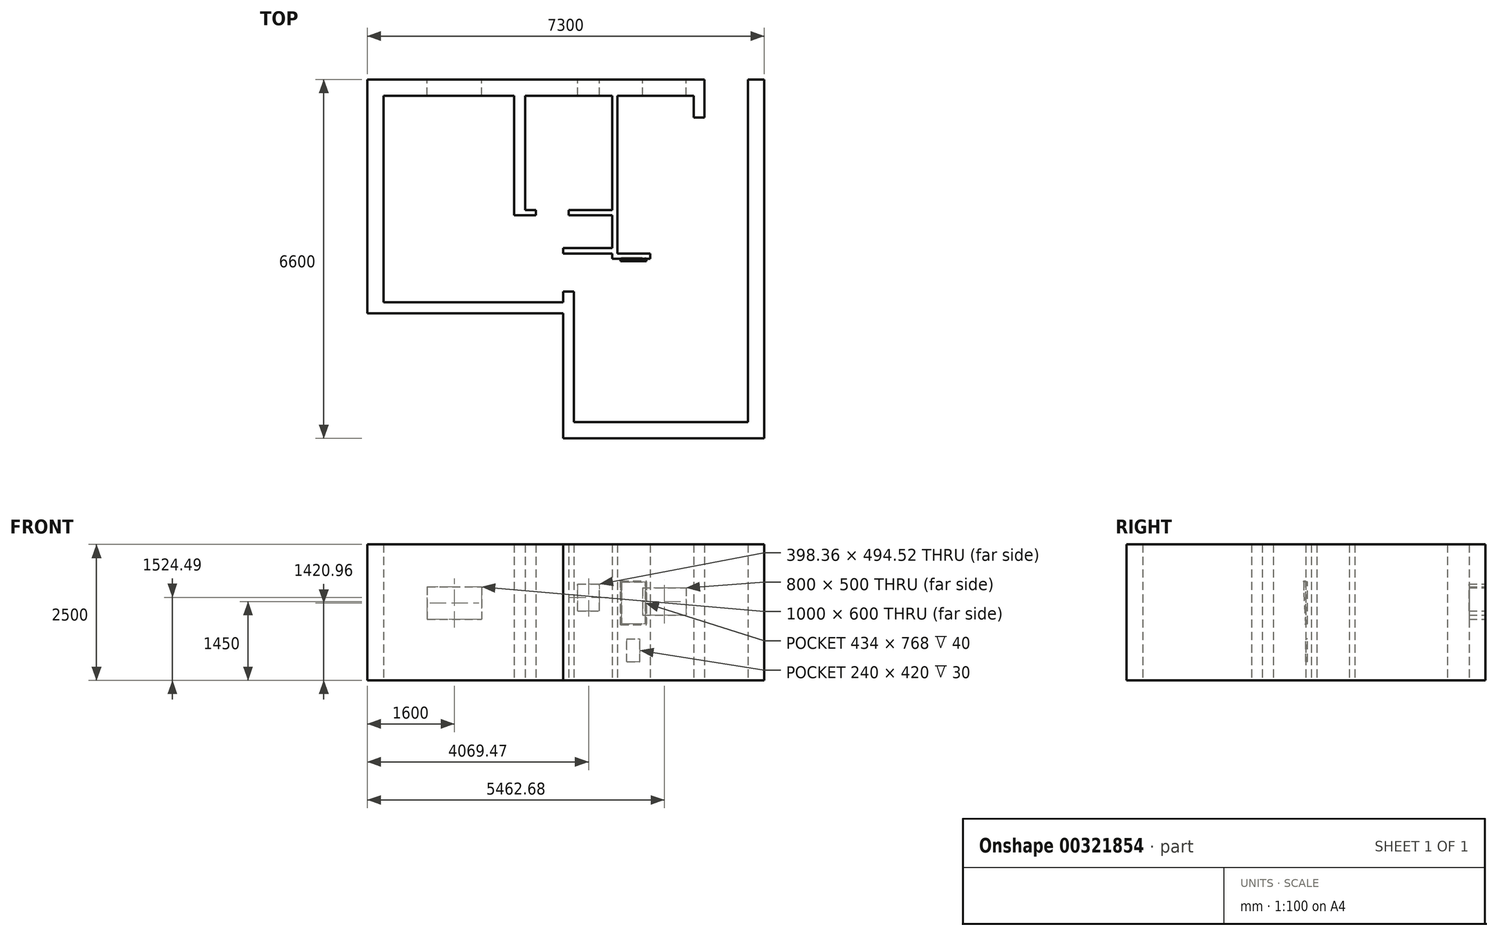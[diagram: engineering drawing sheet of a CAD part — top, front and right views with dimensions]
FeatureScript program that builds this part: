
annotation { "Feature Type Name" : "Feature", "Feature Type Description" : "" }
export const myFeature = defineFeature(function(context is Context, id is Id, definition is map)
    precondition{}
    {
        {
            var Q0;
            Q0=qCreatedBy(makeId("Top.planeOp"),FACE);
            var sketch = newSketch(context, id + "F0", { "sketchPlane" : qUnion([Q0])});
            skLineSegment(sketch, "E0.bottom", {"start": v(0, 0) * mm, "end": v(300, 0) * mm});
            skLineSegment(sketch, "E0.top", {"start": v(0, -5600) * mm, "end": v(300, -5600) * mm});
            skLineSegment(sketch, "E0.left", {"start": v(0, 0) * mm, "end": v(0, -5600) * mm});
            skLineSegment(sketch, "E0.right", {"start": v(300, 0) * mm, "end": v(300, -5600) * mm});
            skLineSegment(sketch, "E1.bottom", {"start": v(300, -5600) * mm, "end": v(-3200, -5600) * mm});
            skLineSegment(sketch, "E1.top", {"start": v(300, -5900) * mm, "end": v(-3200, -5900) * mm});
            skLineSegment(sketch, "E1.left", {"start": v(300, -5600) * mm, "end": v(300, -5900) * mm});
            skLineSegment(sketch, "E1.right", {"start": v(-3200, -5600) * mm, "end": v(-3200, -5900) * mm});
            skLineSegment(sketch, "E2.bottom", {"start": v(-3200, -5900) * mm, "end": v(-3400, -5900) * mm});
            skLineSegment(sketch, "E2.top", {"start": v(-3200, -3200) * mm, "end": v(-3400, -3200) * mm});
            skLineSegment(sketch, "E2.left", {"start": v(-3200, -5900) * mm, "end": v(-3200, -3200) * mm});
            skLineSegment(sketch, "E2.right", {"start": v(-3400, -5900) * mm, "end": v(-3400, -3200) * mm});
            skLineSegment(sketch, "E3.bottom", {"start": v(-3400, -3400) * mm, "end": v(-6700, -3400) * mm});
            skLineSegment(sketch, "E3.top", {"start": v(-3400, -3600) * mm, "end": v(-6700, -3600) * mm});
            skLineSegment(sketch, "E3.left", {"start": v(-3400, -3400) * mm, "end": v(-3400, -3600) * mm});
            skLineSegment(sketch, "E3.right", {"start": v(-6700, -3400) * mm, "end": v(-6700, -3600) * mm});
            skLineSegment(sketch, "E4.bottom", {"start": v(-6700, -3600) * mm, "end": v(-7000, -3600) * mm});
            skLineSegment(sketch, "E4.top", {"start": v(-6700, 400) * mm, "end": v(-7000, 400) * mm});
            skLineSegment(sketch, "E4.left", {"start": v(-6700, -3600) * mm, "end": v(-6700, 400) * mm});
            skLineSegment(sketch, "E4.right", {"start": v(-7000, -3600) * mm, "end": v(-7000, 400) * mm});
            skLineSegment(sketch, "E5.bottom", {"start": v(-7000, 400) * mm, "end": v(-1000, 400) * mm});
            skLineSegment(sketch, "E5.top", {"start": v(-7000, 700) * mm, "end": v(-1000, 700) * mm});
            skLineSegment(sketch, "E5.left", {"start": v(-7000, 400) * mm, "end": v(-7000, 700) * mm});
            skLineSegment(sketch, "E5.right", {"start": v(-1000, 400) * mm, "end": v(-1000, 700) * mm});
            skLineSegment(sketch, "E6.bottom", {"start": v(-4300, 400) * mm, "end": v(-4100, 400) * mm});
            skLineSegment(sketch, "E6.top", {"start": v(-4300, -1800) * mm, "end": v(-4100, -1800) * mm});
            skLineSegment(sketch, "E6.left", {"start": v(-4300, 400) * mm, "end": v(-4300, -1800) * mm});
            skLineSegment(sketch, "E6.right", {"start": v(-4100, 400) * mm, "end": v(-4100, -1800) * mm});
            skLineSegment(sketch, "E7.bottom", {"start": v(-1000, 700) * mm, "end": v(-800, 700) * mm});
            skLineSegment(sketch, "E7.top", {"start": v(-1000, 0) * mm, "end": v(-800, 0) * mm});
            skLineSegment(sketch, "E7.left", {"start": v(-1000, 700) * mm, "end": v(-1000, 0) * mm});
            skLineSegment(sketch, "E7.right", {"start": v(-800, 700) * mm, "end": v(-800, 0) * mm});
            skLineSegment(sketch, "E8.bottom", {"start": v(-4300, -1800) * mm, "end": v(-3900, -1800) * mm});
            skLineSegment(sketch, "E8.top", {"start": v(-4300, -1700) * mm, "end": v(-3900, -1700) * mm});
            skLineSegment(sketch, "E8.left", {"start": v(-4300, -1800) * mm, "end": v(-4300, -1700) * mm});
            skLineSegment(sketch, "E8.right", {"start": v(-3900, -1800) * mm, "end": v(-3900, -1700) * mm});
            skLineSegment(sketch, "E9.bottom", {"start": v(-3300, -1800) * mm, "end": v(-2500, -1800) * mm});
            skLineSegment(sketch, "E9.top", {"start": v(-3300, -1700) * mm, "end": v(-2500, -1700) * mm});
            skLineSegment(sketch, "E9.left", {"start": v(-3300, -1800) * mm, "end": v(-3300, -1700) * mm});
            skLineSegment(sketch, "E9.right", {"start": v(-2500, -1800) * mm, "end": v(-2500, -1700) * mm});
            skLineSegment(sketch, "E10.bottom", {"start": v(-2500, -2500) * mm, "end": v(-2400, -2500) * mm});
            skLineSegment(sketch, "E10.top", {"start": v(-2500, 400) * mm, "end": v(-2400, 400) * mm});
            skLineSegment(sketch, "E10.left", {"start": v(-2500, -2500) * mm, "end": v(-2500, 400) * mm});
            skLineSegment(sketch, "E10.right", {"start": v(-2400, -2500) * mm, "end": v(-2400, 400) * mm});
            skLineSegment(sketch, "E11.bottom", {"start": v(-2500, -2500) * mm, "end": v(-3400, -2500) * mm});
            skLineSegment(sketch, "E11.top", {"start": v(-2500, -2400) * mm, "end": v(-3400, -2400) * mm});
            skLineSegment(sketch, "E11.left", {"start": v(-2500, -2500) * mm, "end": v(-2500, -2400) * mm});
            skLineSegment(sketch, "E11.right", {"start": v(-3400, -2500) * mm, "end": v(-3400, -2400) * mm});
            skLineSegment(sketch, "E12.bottom", {"start": v(-2500, -2500) * mm, "end": v(-1800, -2500) * mm});
            skLineSegment(sketch, "E12.top", {"start": v(-2500, -2600) * mm, "end": v(-1800, -2600) * mm});
            skLineSegment(sketch, "E12.left", {"start": v(-2500, -2500) * mm, "end": v(-2500, -2600) * mm});
            skLineSegment(sketch, "E12.right", {"start": v(-1800, -2500) * mm, "end": v(-1800, -2600) * mm});
            skLineSegment(sketch, "E13.top", {"start": v(0, 700) * mm, "end": v(300, 700) * mm});
            skLineSegment(sketch, "E13.left", {"start": v(0, 0) * mm, "end": v(0, 700) * mm});
            skLineSegment(sketch, "E13.right", {"start": v(300, 0) * mm, "end": v(300, 700) * mm});
            skSolve(sketch);
        }
        {
            var Q0;
            {var subQ3=sQuery(id+"F0.wireOp",EDGE,"E4.top");Q0=makeQuery(id+"F0.imprint","IMPRINT",FACE,{"disambiguationData":[TD([[makeQuery(id+"F0.imprint","IMPRINT",EDGE,{"derivedFrom":subQ3}),-1.0]])]});}
            var Q1;
            Q1=makeQuery(id+"F0.imprint","IMPRINT",FACE,{"disambiguationData":[TD([[makeQuery(id+"F0.imprint","IMPRINT",EDGE,{"derivedFrom":sQuery(id+"F0.wireOp",EDGE,"E3.right")}),-1.0]])]});
            var Q2;
            {var subQ0=sQuery(id+"F0.wireOp",EDGE,"E3.bottom");Q2=makeQuery(id+"F0.imprint","IMPRINT",FACE,{"disambiguationData":[TD([[makeQuery(id+"F0.imprint","IMPRINT",EDGE,{"derivedFrom":subQ0}),1.0]])]});}
            var Q3;
            Q3=makeQuery(id+"F0.imprint","IMPRINT",FACE,{"disambiguationData":[TD([[makeQuery(id+"F0.imprint","IMPRINT",EDGE,{"derivedFrom":sQuery(id+"F0.wireOp",EDGE,"E1.right")}),-1.0]])]});
            var Q4;
            Q4=makeQuery(id+"F0.imprint","IMPRINT",FACE,{"disambiguationData":[TD([[makeQuery(id+"F0.imprint","IMPRINT",EDGE,{"derivedFrom":sQuery(id+"F0.wireOp",EDGE,"E0.top")}),-1.0]])]});
            var Q5;
            Q5=makeQuery(id+"F0.imprint","IMPRINT",FACE,{"disambiguationData":[TD([[makeQuery(id+"F0.imprint","IMPRINT",EDGE,{"derivedFrom":sQuery(id+"F0.wireOp",EDGE,"E0.bottom")}),-1.0]])]});
            var Q6;
            Q6=makeQuery(id+"F0.imprint","IMPRINT",FACE,{"disambiguationData":[TD([[makeQuery(id+"F0.imprint","IMPRINT",EDGE,{"derivedFrom":sQuery(id+"F0.wireOp",EDGE,"E0.bottom")}),1.0]])]});
            var Q7;
            Q7=makeQuery(id+"F0.imprint","IMPRINT",FACE,{"disambiguationData":[TD([[makeQuery(id+"F0.imprint","IMPRINT",EDGE,{"derivedFrom":sQuery(id+"F0.wireOp",EDGE,"E5.right")}),-1.0]])]});
            var Q8;
            Q8=makeQuery(id+"F0.imprint","IMPRINT",FACE,{"disambiguationData":[TD([[makeQuery(id+"F0.imprint","IMPRINT",EDGE,{"derivedFrom":sQuery(id+"F0.wireOp",EDGE,"E10.bottom")}),-1.0]])]});
            var Q9;
            {var subQ1=sQuery(id+"F0.wireOp",EDGE,"E9.right");Q9=makeQuery(id+"F0.imprint","IMPRINT",FACE,{"disambiguationData":[TD([[makeQuery(id+"F0.imprint","IMPRINT",EDGE,{"derivedFrom":subQ1}),-1.0]])]});}
            var Q10;
            {var subQ0=sQuery(id+"F0.wireOp",EDGE,"E11.bottom");Q10=makeQuery(id+"F0.imprint","IMPRINT",FACE,{"disambiguationData":[TD([[makeQuery(id+"F0.imprint","IMPRINT",EDGE,{"derivedFrom":subQ0}),-1.0]])]});}
            var Q11;
            Q11=makeQuery(id+"F0.imprint","IMPRINT",FACE,{"disambiguationData":[TD([[makeQuery(id+"F0.imprint","IMPRINT",EDGE,{"derivedFrom":sQuery(id+"F0.wireOp",EDGE,"E9.bottom")}),1.0]])]});
            var Q12;
            {var subQ0=sQuery(id+"F0.wireOp",EDGE,"E8.bottom");Q12=makeQuery(id+"F0.imprint","IMPRINT",FACE,{"disambiguationData":[TD([[makeQuery(id+"F0.imprint","IMPRINT",EDGE,{"derivedFrom":subQ0}),1.0]])]});}
            var Q13;
            {var subQ0=sQuery(id+"F0.wireOp",EDGE,"E6.top");Q13=makeQuery(id+"F0.imprint","IMPRINT",FACE,{"disambiguationData":[TD([[makeQuery(id+"F0.imprint","IMPRINT",EDGE,{"derivedFrom":subQ0}),1.0]])]});}
            var Q14;
            {var subQ0=sQuery(id+"F0.wireOp",EDGE,"E6.left");var subQ1=sQuery(id+"F0.wireOp",EDGE,"E5.bottom");var subQ2=makeQuery(id+"F0.imprint","INTERSECT",VERTEX,{"derivedFrom":[subQ1,subQ0]});Q14=makeQuery(id+"F0.imprint","IMPRINT",FACE,{"disambiguationData":[TD([[makeQuery(id+"F0.imprint","IMPRINT",EDGE,{"disambiguationData":[TD([[subQ2,-1.0]])],"derivedFrom":subQ1}),-1.0]])]});}
            extrude(context, id + "F1", {"entities" : qUnion([Q0, Q1, Q2, Q3, Q4, Q5, Q6, Q7, Q8, Q9, Q10, Q11, Q12, Q13, Q14]), "depth" : 2500 * mm});
        }
        {
            var Q0;
            Q0=makeQuery(id+"F1.opExtrude","SWEPT_FACE",FACE,{"disambiguationData":[OSD([sQuery(id+"F0.wireOp",EDGE,"E5.top"),sQuery(id+"F0.wireOp",EDGE,"E7.bottom")])]});
            var sketch = newSketch(context, id + "F2", { "sketchPlane" : qUnion([Q0])});
            skLineSegment(sketch, "E14", {"start": v(5400, 0) * mm, "end": v(5400, 2500) * mm, "construction": true});
            skLineSegment(sketch, "E15", {"start": v(1537.32, 0) * mm, "end": v(1537.32, 2500) * mm, "construction": true});
            skLineSegment(sketch, "E16.bottom", {"start": v(5900, 1720.96) * mm, "end": v(4900, 1720.96) * mm});
            skLineSegment(sketch, "E16.top", {"start": v(5900, 1120.96) * mm, "end": v(4900, 1120.96) * mm});
            skLineSegment(sketch, "E16.left", {"start": v(5900, 1720.96) * mm, "end": v(5900, 1120.96) * mm});
            skLineSegment(sketch, "E16.right", {"start": v(4900, 1720.96) * mm, "end": v(4900, 1120.96) * mm});
            skPoint(sketch, "E16.middle", {"position": v(5400, 1420.96) * mm});
            skLineSegment(sketch, "E17.bottom", {"start": v(1937.32, 1700) * mm, "end": v(1137.32, 1700) * mm});
            skLineSegment(sketch, "E17.top", {"start": v(1937.32, 1200) * mm, "end": v(1137.32, 1200) * mm});
            skLineSegment(sketch, "E17.left", {"start": v(1937.32, 1700) * mm, "end": v(1937.32, 1200) * mm});
            skLineSegment(sketch, "E17.right", {"start": v(1137.32, 1700) * mm, "end": v(1137.32, 1200) * mm});
            skPoint(sketch, "E17.middle", {"position": v(1537.32, 1450) * mm});
            skLineSegment(sketch, "E18", {"start": v(2930.53, 0) * mm, "end": v(2930.53, 2500) * mm, "construction": true});
            skLineSegment(sketch, "E19.bottom", {"start": v(3129.7, 1277.23) * mm, "end": v(2731.35, 1277.23) * mm});
            skLineSegment(sketch, "E19.top", {"start": v(3129.7, 1771.75) * mm, "end": v(2731.35, 1771.75) * mm});
            skLineSegment(sketch, "E19.left", {"start": v(3129.7, 1277.23) * mm, "end": v(3129.7, 1771.75) * mm});
            skLineSegment(sketch, "E19.right", {"start": v(2731.35, 1277.23) * mm, "end": v(2731.35, 1771.75) * mm});
            skPoint(sketch, "E19.middle", {"position": v(2930.53, 1524.49) * mm});
            skSolve(sketch);
        }
        {
            var Q0;
            Q0 = qSketchRegion(id + "F2", true);
            extrude(context, id + "F3", {"entities" : qUnion([Q0]), "operationType" : NewBodyOperationType.REMOVE, "oppositeDirection" : true, "depth" : 990 * mm});
        }
        {
            var Q0;
            Q0=makeQuery(id+"F1.opExtrude","SWEPT_FACE",FACE,{"disambiguationData":[OSD([sQuery(id+"F0.wireOp",EDGE,"E12.top")])]});
            var sketch = newSketch(context, id + "F4", { "sketchPlane" : qUnion([Q0])});
            skLineSegment(sketch, "E20.bottom", {"start": v(-2230, 340) * mm, "end": v(-1990, 340) * mm});
            skLineSegment(sketch, "E20.top", {"start": v(-2230, 760) * mm, "end": v(-1990, 760) * mm});
            skLineSegment(sketch, "E20.left", {"start": v(-2230, 340) * mm, "end": v(-2230, 760) * mm});
            skLineSegment(sketch, "E20.right", {"start": v(-1990, 340) * mm, "end": v(-1990, 760) * mm});
            skLineSegment(sketch, "E21.bottom", {"start": v(-2344, 1020) * mm, "end": v(-1870, 1020) * mm});
            skLineSegment(sketch, "E21.top", {"start": v(-2344, 1828) * mm, "end": v(-1870, 1828) * mm});
            skLineSegment(sketch, "E21.left", {"start": v(-2344, 1020) * mm, "end": v(-2344, 1828) * mm});
            skLineSegment(sketch, "E21.right", {"start": v(-1870, 1020) * mm, "end": v(-1870, 1828) * mm});
            skSolve(sketch);
        }
        {
            var Q0;
            Q0 = qSketchRegion(id + "F4", true);
            extrude(context, id + "F5", {"entities" : qUnion([Q0]), "operationType" : NewBodyOperationType.REMOVE, "oppositeDirection" : true, "depth" : 30 * mm, "offsetDistance" : 25 * mm});
        }
        {
            var Q0;
            Q0=makeQuery(id+"F5.boolean.opBoolean","COPY",FACE,{"derivedFrom":makeQuery(id+"F5.opExtrude","CAP_FACE",FACE,{"disambiguationData":[OSD([sQuery(id+"F4.wireOp",EDGE,"E21.bottom"),sQuery(id+"F4.wireOp",EDGE,"E21.top"),sQuery(id+"F4.wireOp",EDGE,"E21.left"),sQuery(id+"F4.wireOp",EDGE,"E21.right")])],"isStart":false})});
            var sketch = newSketch(context, id + "F6", { "sketchPlane" : qUnion([Q0])});
            skLineSegment(sketch, "E22.bottom", {"start": v(-2344, 1020) * mm, "end": v(-1870, 1020) * mm});
            skLineSegment(sketch, "E22.top", {"start": v(-2344, 1040) * mm, "end": v(-1870, 1040) * mm});
            skLineSegment(sketch, "E22.left", {"start": v(-2344, 1020) * mm, "end": v(-2344, 1040) * mm});
            skLineSegment(sketch, "E22.right", {"start": v(-1870, 1020) * mm, "end": v(-1870, 1040) * mm});
            skSolve(sketch);
        }
        {
            var Q0;
            Q0=makeQuery(id+"F6.imprint","IMPRINT",FACE,{"disambiguationData":[TD([[makeQuery(id+"F6.imprint","IMPRINT",EDGE,{"derivedFrom":sQuery(id+"F6.wireOp",EDGE,"E22.bottom")}),1.0]])]});
            extrude(context, id + "F7", {"entities" : qUnion([Q0]), "depth" : 40 * mm, "offsetDistance" : 25 * mm});
        }
        {
            var Q0;
            Q0=makeQuery(id+"F5.boolean.opBoolean","COPY",FACE,{"derivedFrom":makeQuery(id+"F5.opExtrude","CAP_FACE",FACE,{"disambiguationData":[OSD([sQuery(id+"F4.wireOp",EDGE,"E21.bottom"),sQuery(id+"F4.wireOp",EDGE,"E21.top"),sQuery(id+"F4.wireOp",EDGE,"E21.left"),sQuery(id+"F4.wireOp",EDGE,"E21.right")])],"isStart":false})});
            var sketch = newSketch(context, id + "F8", { "sketchPlane" : qUnion([Q0])});
            skLineSegment(sketch, "E23.bottom", {"start": v(-2344, 1828) * mm, "end": v(-1870, 1828) * mm});
            skLineSegment(sketch, "E23.top", {"start": v(-2344, 1808) * mm, "end": v(-1870, 1808) * mm});
            skLineSegment(sketch, "E23.left", {"start": v(-2344, 1828) * mm, "end": v(-2344, 1808) * mm});
            skLineSegment(sketch, "E23.right", {"start": v(-1870, 1828) * mm, "end": v(-1870, 1808) * mm});
            skSolve(sketch);
        }
        {
            var Q0;
            Q0 = qSketchRegion(id + "F8", true);
            extrude(context, id + "F9", {"entities" : qUnion([Q0]), "operationType" : NewBodyOperationType.ADD, "depth" : 70 * mm, "offsetDistance" : 25 * mm});
        }
        {
            var Q0;
            Q0=makeQuery(id+"F5.boolean.opBoolean","COPY",FACE,{"derivedFrom":makeQuery(id+"F5.opExtrude","SWEPT_FACE",FACE,{"disambiguationData":[OSD([sQuery(id+"F4.wireOp",EDGE,"E21.left")])]})});
            var sketch = newSketch(context, id + "F10", { "sketchPlane" : qUnion([Q0])});
            skLineSegment(sketch, "E24", {"start": v(-2609.52, 1040) * mm, "end": v(-2570, 1040) * mm});
            skLineSegment(sketch, "E25", {"start": v(-2570, 1040) * mm, "end": v(-2570, 1808) * mm});
            skLineSegment(sketch, "E26", {"start": v(-2570, 1808) * mm, "end": v(-2640.1, 1808) * mm});
            skLineSegment(sketch, "E27", {"start": v(-2640.1, 1808) * mm, "end": v(-2640.1, 1608) * mm});
            skLineSegment(sketch, "E28", {"start": v(-2640.1, 1608) * mm, "end": v(-2609.52, 1040) * mm});
            skSolve(sketch);
        }
        {
            var Q0;
            Q0 = qSketchRegion(id + "F10", true);
            extrude(context, id + "F11", {"entities" : qUnion([Q0]), "operationType" : NewBodyOperationType.ADD, "depth" : 20 * mm, "offsetDistance" : 25 * mm});
        }
        {
            var Q0;
            Q0 = qSketchRegion(id + "F10", true);
            extrude(context, id + "F12", {"entities" : qUnion([Q0]), "operationType" : NewBodyOperationType.ADD, "depth" : 474 * mm, "offsetDistance" : 25 * mm, "hasSecondDirection" : true, "secondDirectionOppositeDirection" : false, "secondDirectionDepth" : 454 * mm});
        }
    });
